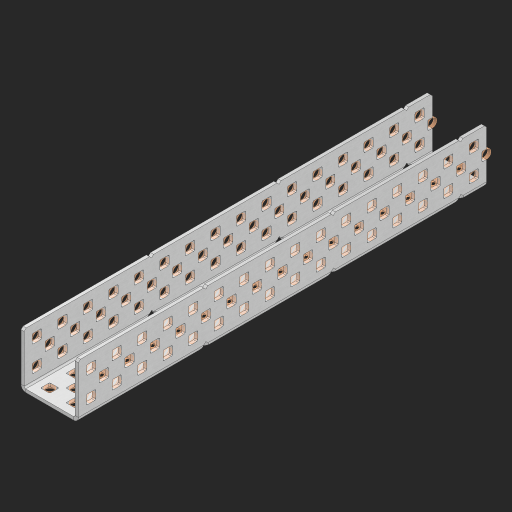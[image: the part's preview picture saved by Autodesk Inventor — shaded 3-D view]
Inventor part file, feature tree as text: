
AUTODESK INVENTOR PART (.ipt)
format: ipt  version: 2023 (Build 270158000, 158)  size: 1,927,168 bytes
history: native  units: in
note: dims shown in document units (in); Inventor stores cm internally (conversion verified against a paired STEP export)
features: other x198, extrude x190, sheet_metal_op x8, sketch x7, mirror x3, pattern_linear x2, chamfer x1
ambient origin geometry x8: Origin, YZ Plane, XZ Plane, XY Plane, X Axis, Y Axis, Z Axis, Center Point
bodies: Solid1 (feature_tree), Body (feature_tree)
feature tree (409):
  sheet_metal_op  "Flanges"
  sheet_metal_op  "Body Pattern"
  pattern_linear  "Center Pattern"  Spacing1=1.0in  [1 undecoded]
  other  "Arc Length"
  mirror  "Notch Mirror"
  pattern_linear  "Notch Pattern"  Spacing1=0.25in  [1 undecoded]
  other  "Diagonal Plane"
  mirror  "Flange 1"
  mirror  "Flange 2"
  chamfer  "End Chamfer"
  sketch  "Sketch1"  dims[d0=1.0in]
  other  "Plate1"
  sketch  "Sketch2"  dims[d1=8.0in]
  other  "Plate2"
  sheet_metal_op  "Bend1"
  sheet_metal_op  "Corner1"
  sketch  "Sketch8"  dims[d2=0.0625in]
  sketch  "Sketch9"  dims[d3=0.0625in]
  other  "Srf91"
  sheet_metal_op  "Body Pattern Sketch"
  other  "Srf92"
  sketch  "Sketch13"  dims[d4=0.0312in]
  sketch  "Sketch15"  dims[d5=0.125in]
  sketch  "Sketch16"  dims[d6=0.0625in d7=1.0in d8=90.0deg d9=0.0312in d10=0.25in d11=0.0625in d12=0.0625in d49=0.182in d50=0.02in d52=0.25in d53=0.0625in d54=0.0in d55=0.172in d56=1.0in d57=0.0in d60=6.2992in d62=0.5in d63=0.7874in d65=0.5in d85=0.1473in d86=0.1782in d88=0.04in d89=0.0625in d90=0.0in d91=0.04in d92=0.0491in d95=2.5in d96=0.04in d97=0.25in d98=45.0deg d99=0.25in d102=2.497in d106=0.182in d107=0.02in d108=0.5in d110=0.0625in d111=0.0in d112=0.172in d113=0.5in d114=0.0in d117=0.5in d118=0.5in d131=0.25in d132=0.25in]
  other  "Srf786"
  other  "Srf889"
  other  "Srf890"
  other  "Srf891"
  other  "Srf892"
  other  "Srf893"
  other  "Srf894"
  other  "Srf895"
  other  "Srf896"
  other  "Srf996"
  other  "Srf997"
  other  "Srf998"
  other  "Srf999"
  other  "Srf1000"
  other  "Srf1255"
  other  "Srf1256"
  other  "Srf1315"
  other  "Srf1316"
  other  "Srf1317"
  other  "Srf1325"
  other  "Srf1326"
  other  "Srf1327"
  other  "Srf1328"
  other  "Srf1329"
  other  "Srf1330"
  other  "Srf1331"
  other  "Srf1332"
  other  "Srf1338"
  other  "Srf1339"
  other  "Srf1340"
  other  "Srf1341"
  other  "Srf1342"
  other  "Srf1369"
  other  "Srf1370"
  other  "Srf1374"
  other  "Srf1375"
  other  "Srf1376"
  other  "Srf1384"
  other  "Srf1385"
  other  "Srf1386"
  other  "Srf1387"
  other  "Srf1388"
  other  "Srf1389"
  other  "Srf1390"
  other  "Srf1391"
  other  "Srf1397"
  other  "Srf1398"
  other  "Srf1399"
  other  "Srf1400"
  other  "Srf1401"
  other  "Srf1428"
  other  "Srf1429"
  other  "Srf1433"
  other  "Srf1434"
  other  "Srf1473"
  other  "Srf1474"
  other  "Srf1475"
  other  "Srf1476"
  other  "Srf1477"
  other  "Srf1478"
  other  "Srf1479"
  other  "Srf1480"
  other  "Srf1481"
  other  "Srf1482"
  other  "Srf1483"
  other  "Srf1484"
  other  "Srf1485"
  other  "Srf1486"
  other  "Srf1487"
  other  "Srf1488"
  other  "Srf1500"
  other  "Srf1501"
  other  "Srf1502"
  other  "Srf1503"
  other  "Srf1504"
  other  "Srf1505"
  other  "Srf1506"
  other  "Srf1507"
  other  "Srf1508"
  other  "Srf1509"
  other  "Srf1510"
  other  "Srf1511"
  other  "Srf1512"
  other  "Srf1513"
  other  "Srf1514"
  other  "Srf1515"
  other  "Srf1516"
  other  "Srf1517"
  other  "Srf1518"
  other  "Srf1519"
  other  "Srf1520"
  other  "Srf1521"
  other  "Srf1522"
  other  "Srf1523"
  other  "Srf1524"
  other  "Srf1525"
  other  "Srf1526"
  other  "Srf1527"
  other  "Srf1528"
  other  "Srf1529"
  other  "Srf1538"
  other  "Srf1539"
  other  "Srf1540"
  other  "Srf1541"
  other  "Srf1542"
  other  "Srf1543"
  other  "Srf1544"
  other  "Srf1545"
  other  "Srf1546"
  other  "Srf1547"
  other  "Srf1548"
  other  "Srf1549"
  other  "Srf1550"
  other  "Srf1551"
  other  "Srf1552"
  other  "Srf1553"
  other  "Srf1554"
  other  "Srf1555"
  other  "Srf1556"
  other  "Srf1557"
  other  "Srf1558"
  other  "Srf1559"
  other  "Srf1560"
  other  "Srf1561"
  other  "Srf1562"
  other  "Srf1563"
  other  "Srf1564"
  other  "Srf1565"
  other  "Srf1566"
  other  "Srf1567"
  other  "Srf1576"
  other  "Srf1577"
  other  "Srf1578"
  other  "Srf1579"
  other  "Srf1580"
  other  "Srf1581"
  other  "Srf1582"
  other  "Srf1583"
  other  "Srf1584"
  other  "Srf1585"
  other  "Srf1586"
  other  "Srf1587"
  other  "Srf1588"
  other  "Srf1589"
  other  "Srf1590"
  other  "Srf1591"
  other  "Srf1592"
  other  "Srf1593"
  other  "Srf1594"
  other  "Srf1595"
  other  "Srf1596"
  other  "Srf1597"
  other  "Srf1598"
  other  "Srf1599"
  other  "Srf1600"
  other  "Srf1601"
  other  "Srf1602"
  other  "Srf1603"
  other  "Srf1604"
  other  "Srf1605"
  other  "Srf1614"
  other  "Srf1615"
  other  "Srf1616"
  other  "Srf1617"
  other  "Srf1618"
  other  "Srf1619"
  other  "Srf1620"
  other  "Srf1621"
  other  "Srf1622"
  other  "Srf1623"
  other  "Srf1624"
  other  "Srf1625"
  other  "Srf1626"
  other  "Srf1627"
  other  "Srf1628"
  other  "Srf1629"
  other  "Srf1630"
  other  "Srf1631"
  other  "Srf1632"
  other  "Srf1633"
  other  "Srf1634"
  other  "Srf1635"
  other  "Srf1636"
  other  "Srf1637"
  other  "Srf1638"
  other  "Srf1639"
  other  "Srf1640"
  other  "Srf1641"
  other  "Srf1642"
  other  "Srf1643"
  sheet_metal_op  "Body Stamp"
  sheet_metal_op  "Body Circle"
  other  "Center Stamp"
  other  "Center Circle"
  sheet_metal_op  "Notch"
  extrude  "ExtrusionSrf92"  Depth=0.0625in
  extrude  "ExtrusionSrf889"  Depth=0.0625in
  extrude  "ExtrusionSrf890"  Depth=0.182in
  extrude  "ExtrusionSrf891"  Depth=0.02in
  extrude  "ExtrusionSrf892"  Depth=0.25in
  extrude  "ExtrusionSrf893"  Depth=0.0625in
  extrude  "ExtrusionSrf894"  TaperAngle=0.0deg  [1 undecoded]
  extrude  "ExtrusionSrf895"  Depth=0.25in
  extrude  "ExtrusionSrf896"  Depth=1.0in TaperAngle=0.0deg
  extrude  "ExtrusionSrf996"  Depth=0.25in
  extrude  "ExtrusionSrf997"  Depth=0.5in
  extrude  "ExtrusionSrf998"  Depth=0.25in
  extrude  "ExtrusionSrf999"  Depth=0.25in
  extrude  "ExtrusionSrf1000"  Depth=0.25in
  extrude  "ExtrusionSrf1255"  Depth=0.0625in
  extrude  "ExtrusionSrf1256"  TaperAngle=0.0deg  [1 undecoded]
  extrude  "ExtrusionSrf1315"  Depth=0.25in
  extrude  "ExtrusionSrf1316"  Depth=0.25in
  extrude  "ExtrusionSrf1355"  Depth=2.5in
  extrude  "ExtrusionSrf1356"  Depth=0.25in TaperAngle=45.0deg
  extrude  "ExtrusionSrf1357"  Depth=0.25in
  extrude  "ExtrusionSrf1358"  Depth=0.25in
  extrude  "ExtrusionSrf1359"  Depth=0.182in
  extrude  "ExtrusionSrf1360"  Depth=0.02in
  extrude  "ExtrusionSrf1361"  Depth=0.5in
  extrude  "ExtrusionSrf1362"  Depth=0.0625in
  extrude  "ExtrusionSrf1363"  TaperAngle=0.0deg  [1 undecoded]
  extrude  "ExtrusionSrf1364"  Depth=0.25in
  extrude  "ExtrusionSrf1365"  Depth=0.5in TaperAngle=0.0deg
  extrude  "ExtrusionSrf1366"  Depth=0.5in
  extrude  "ExtrusionSrf1367"  Depth=0.5in
  extrude  "ExtrusionSrf1368"  Depth=0.25in
  extrude  "ExtrusionSrf1369"  Depth=0.25in
  extrude  "ExtrusionSrf1370"  [1 undecoded]
  extrude  "ExtrusionSrf1374"  [1 undecoded]
  extrude  "ExtrusionSrf1375"  [1 undecoded]
  extrude  "ExtrusionSrf1414"  [1 undecoded]
  extrude  "ExtrusionSrf1415"  [1 undecoded]
  extrude  "ExtrusionSrf1416"  [1 undecoded]
  extrude  "ExtrusionSrf1417"  [1 undecoded]
  extrude  "ExtrusionSrf1418"  [1 undecoded]
  extrude  "ExtrusionSrf1419"  [1 undecoded]
  extrude  "ExtrusionSrf1420"  [1 undecoded]
  extrude  "ExtrusionSrf1421"  [1 undecoded]
  extrude  "ExtrusionSrf1422"  [1 undecoded]
  extrude  "ExtrusionSrf1423"  [1 undecoded]
  extrude  "ExtrusionSrf1424"  [1 undecoded]
  extrude  "ExtrusionSrf1425"  [1 undecoded]
  extrude  "ExtrusionSrf1426"  [1 undecoded]
  extrude  "ExtrusionSrf1427"  [1 undecoded]
  extrude  "ExtrusionSrf1428"  [1 undecoded]
  extrude  "ExtrusionSrf1429"  [1 undecoded]
  extrude  "ExtrusionSrf1433"  [1 undecoded]
  extrude  "ExtrusionSrf1434"  [1 undecoded]
  extrude  "ExtrusionSrf1473"  [1 undecoded]
  extrude  "ExtrusionSrf1474"  [1 undecoded]
  extrude  "ExtrusionSrf1475"  [1 undecoded]
  extrude  "ExtrusionSrf1476"  [1 undecoded]
  extrude  "ExtrusionSrf1477"  [1 undecoded]
  extrude  "ExtrusionSrf1478"  [1 undecoded]
  extrude  "ExtrusionSrf1479"  [1 undecoded]
  extrude  "ExtrusionSrf1480"  [1 undecoded]
  extrude  "ExtrusionSrf1481"  [1 undecoded]
  extrude  "ExtrusionSrf1482"  [1 undecoded]
  extrude  "ExtrusionSrf1483"  [1 undecoded]
  extrude  "ExtrusionSrf1484"  [1 undecoded]
  extrude  "ExtrusionSrf1485"  [1 undecoded]
  extrude  "ExtrusionSrf1486"  [1 undecoded]
  extrude  "ExtrusionSrf1487"  [1 undecoded]
  extrude  "ExtrusionSrf1488"  [1 undecoded]
  extrude  "ExtrusionSrf1500"  [1 undecoded]
  extrude  "ExtrusionSrf1501"  [1 undecoded]
  extrude  "ExtrusionSrf1502"  [1 undecoded]
  extrude  "ExtrusionSrf1503"  [1 undecoded]
  extrude  "ExtrusionSrf1504"  [1 undecoded]
  extrude  "ExtrusionSrf1505"  [1 undecoded]
  extrude  "ExtrusionSrf1506"  [1 undecoded]
  extrude  "ExtrusionSrf1507"  [1 undecoded]
  extrude  "ExtrusionSrf1508"  [1 undecoded]
  extrude  "ExtrusionSrf1509"  [1 undecoded]
  extrude  "ExtrusionSrf1510"  [1 undecoded]
  extrude  "ExtrusionSrf1511"  [1 undecoded]
  extrude  "ExtrusionSrf1512"  [1 undecoded]
  extrude  "ExtrusionSrf1513"  [1 undecoded]
  extrude  "ExtrusionSrf1514"  [1 undecoded]
  extrude  "ExtrusionSrf1515"  [1 undecoded]
  extrude  "ExtrusionSrf1516"  [1 undecoded]
  extrude  "ExtrusionSrf1517"  [1 undecoded]
  extrude  "ExtrusionSrf1518"  [1 undecoded]
  extrude  "ExtrusionSrf1519"  [1 undecoded]
  extrude  "ExtrusionSrf1520"  [1 undecoded]
  extrude  "ExtrusionSrf1521"  [1 undecoded]
  extrude  "ExtrusionSrf1522"  [1 undecoded]
  extrude  "ExtrusionSrf1523"  [1 undecoded]
  extrude  "ExtrusionSrf1524"  [1 undecoded]
  extrude  "ExtrusionSrf1525"  [1 undecoded]
  extrude  "ExtrusionSrf1526"  [1 undecoded]
  extrude  "ExtrusionSrf1527"  [1 undecoded]
  extrude  "ExtrusionSrf1528"  [1 undecoded]
  extrude  "ExtrusionSrf1529"  [1 undecoded]
  extrude  "ExtrusionSrf1538"  [1 undecoded]
  extrude  "ExtrusionSrf1539"  [1 undecoded]
  extrude  "ExtrusionSrf1540"  [1 undecoded]
  extrude  "ExtrusionSrf1541"  [1 undecoded]
  extrude  "ExtrusionSrf1542"  [1 undecoded]
  extrude  "ExtrusionSrf1543"  [1 undecoded]
  extrude  "ExtrusionSrf1544"  [1 undecoded]
  extrude  "ExtrusionSrf1545"  [1 undecoded]
  extrude  "ExtrusionSrf1546"  [1 undecoded]
  extrude  "ExtrusionSrf1547"  [1 undecoded]
  extrude  "ExtrusionSrf1548"  [1 undecoded]
  extrude  "ExtrusionSrf1549"  [1 undecoded]
  extrude  "ExtrusionSrf1550"  [1 undecoded]
  extrude  "ExtrusionSrf1551"  [1 undecoded]
  extrude  "ExtrusionSrf1552"  [1 undecoded]
  extrude  "ExtrusionSrf1553"  [1 undecoded]
  extrude  "ExtrusionSrf1554"  [1 undecoded]
  extrude  "ExtrusionSrf1555"  [1 undecoded]
  extrude  "ExtrusionSrf1556"  [1 undecoded]
  extrude  "ExtrusionSrf1557"  [1 undecoded]
  extrude  "ExtrusionSrf1558"  [1 undecoded]
  extrude  "ExtrusionSrf1559"  [1 undecoded]
  extrude  "ExtrusionSrf1560"  [1 undecoded]
  extrude  "ExtrusionSrf1561"  [1 undecoded]
  extrude  "ExtrusionSrf1562"  [1 undecoded]
  extrude  "ExtrusionSrf1563"  [1 undecoded]
  extrude  "ExtrusionSrf1564"  [1 undecoded]
  extrude  "ExtrusionSrf1565"  [1 undecoded]
  extrude  "ExtrusionSrf1566"  [1 undecoded]
  extrude  "ExtrusionSrf1567"  [1 undecoded]
  extrude  "ExtrusionSrf1576"  [1 undecoded]
  extrude  "ExtrusionSrf1577"  [1 undecoded]
  extrude  "ExtrusionSrf1578"  [1 undecoded]
  extrude  "ExtrusionSrf1579"  [1 undecoded]
  extrude  "ExtrusionSrf1580"  [1 undecoded]
  extrude  "ExtrusionSrf1581"  [1 undecoded]
  extrude  "ExtrusionSrf1582"  [1 undecoded]
  extrude  "ExtrusionSrf1583"  [1 undecoded]
  extrude  "ExtrusionSrf1584"  [1 undecoded]
  extrude  "ExtrusionSrf1585"  [1 undecoded]
  extrude  "ExtrusionSrf1586"  [1 undecoded]
  extrude  "ExtrusionSrf1587"  [1 undecoded]
  extrude  "ExtrusionSrf1588"  [1 undecoded]
  extrude  "ExtrusionSrf1589"  [1 undecoded]
  extrude  "ExtrusionSrf1590"  [1 undecoded]
  extrude  "ExtrusionSrf1591"  [1 undecoded]
  extrude  "ExtrusionSrf1592"  [1 undecoded]
  extrude  "ExtrusionSrf1593"  [1 undecoded]
  extrude  "ExtrusionSrf1594"  [1 undecoded]
  extrude  "ExtrusionSrf1595"  [1 undecoded]
  extrude  "ExtrusionSrf1596"  [1 undecoded]
  extrude  "ExtrusionSrf1597"  [1 undecoded]
  extrude  "ExtrusionSrf1598"  [1 undecoded]
  extrude  "ExtrusionSrf1599"  [1 undecoded]
  extrude  "ExtrusionSrf1600"  [1 undecoded]
  extrude  "ExtrusionSrf1601"  [1 undecoded]
  extrude  "ExtrusionSrf1602"  [1 undecoded]
  extrude  "ExtrusionSrf1603"  [1 undecoded]
  extrude  "ExtrusionSrf1604"  [1 undecoded]
  extrude  "ExtrusionSrf1605"  [1 undecoded]
  extrude  "ExtrusionSrf1614"  [1 undecoded]
  extrude  "ExtrusionSrf1615"  [1 undecoded]
  extrude  "ExtrusionSrf1616"  [1 undecoded]
  extrude  "ExtrusionSrf1617"  [1 undecoded]
  extrude  "ExtrusionSrf1618"  [1 undecoded]
  extrude  "ExtrusionSrf1619"  [1 undecoded]
  extrude  "ExtrusionSrf1620"  [1 undecoded]
  extrude  "ExtrusionSrf1621"  [1 undecoded]
  extrude  "ExtrusionSrf1622"  [1 undecoded]
  extrude  "ExtrusionSrf1623"  [1 undecoded]
  extrude  "ExtrusionSrf1624"  [1 undecoded]
  extrude  "ExtrusionSrf1625"  [1 undecoded]
  extrude  "ExtrusionSrf1626"  [1 undecoded]
  extrude  "ExtrusionSrf1627"  [1 undecoded]
  extrude  "ExtrusionSrf1628"  [1 undecoded]
  extrude  "ExtrusionSrf1629"  [1 undecoded]
  extrude  "ExtrusionSrf1630"  [1 undecoded]
  extrude  "ExtrusionSrf1631"  [1 undecoded]
  extrude  "ExtrusionSrf1632"  [1 undecoded]
  extrude  "ExtrusionSrf1633"  [1 undecoded]
  extrude  "ExtrusionSrf1634"  [1 undecoded]
  extrude  "ExtrusionSrf1635"  [1 undecoded]
  extrude  "ExtrusionSrf1636"  [1 undecoded]
  extrude  "ExtrusionSrf1637"  [1 undecoded]
  extrude  "ExtrusionSrf1638"  [1 undecoded]
  extrude  "ExtrusionSrf1639"  [1 undecoded]
  extrude  "ExtrusionSrf1640"  [1 undecoded]
  extrude  "ExtrusionSrf1641"  [1 undecoded]
  extrude  "ExtrusionSrf1642"  [1 undecoded]
  extrude  "ExtrusionSrf1643"  [1 undecoded]
note: 162 required parameter values undecoded (feature->parameter linkage not recoverable at this tier; creation-order binding heuristic only, values carry confidence <= 0.55)
